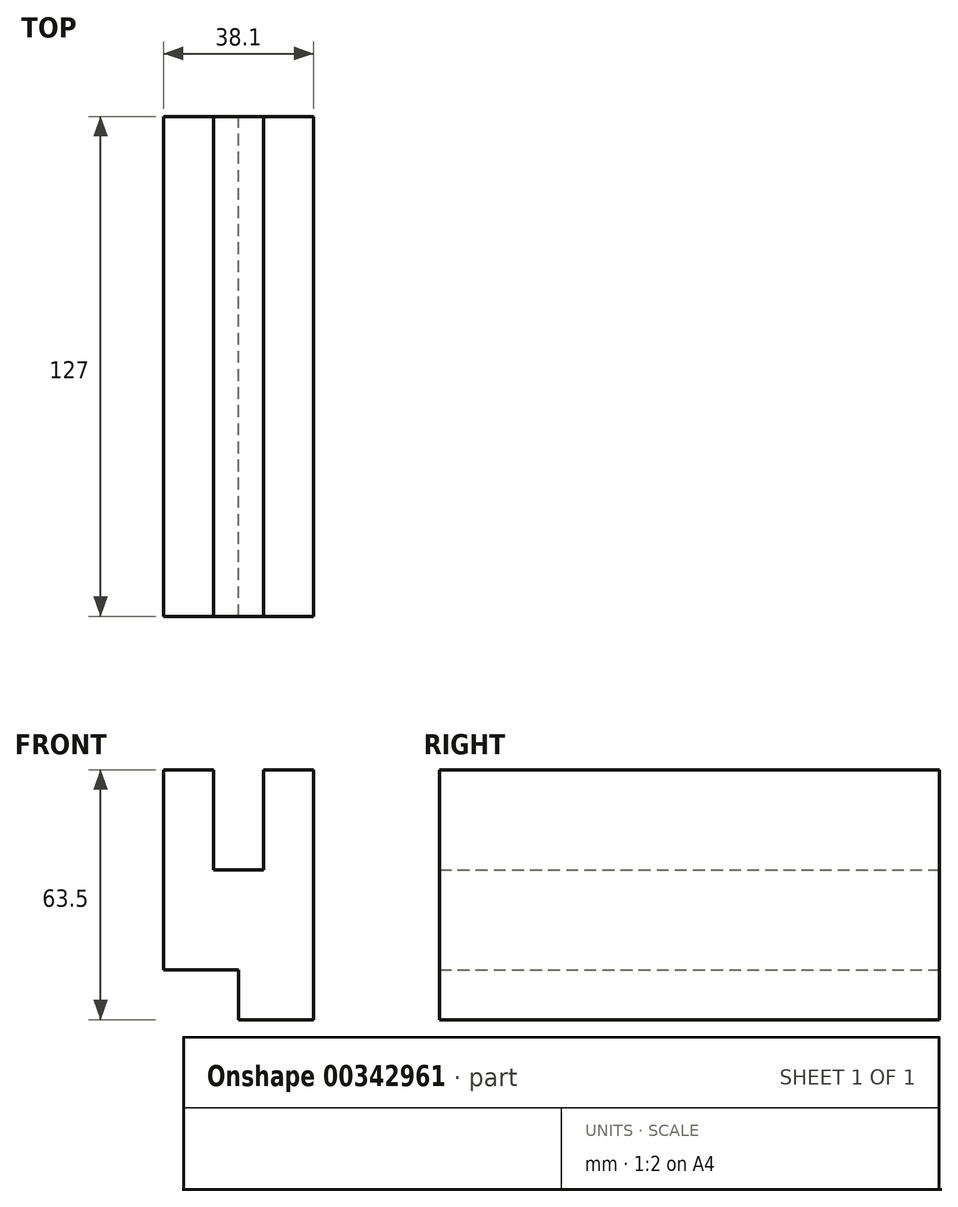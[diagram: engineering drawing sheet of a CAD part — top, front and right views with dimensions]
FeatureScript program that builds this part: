
annotation { "Feature Type Name" : "Feature", "Feature Type Description" : "" }
export const myFeature = defineFeature(function(context is Context, id is Id, definition is map)
    precondition{}
    {
        {
            var Q0;
            Q0=qCreatedBy(makeId("Front.planeOp"),FACE);
            var sketch = newSketch(context, id + "F0", { "sketchPlane" : qUnion([Q0])});
            skLineSegment(sketch, "E0", {"start": v(-56.74, -21.71) * mm, "end": v(-37.7, -21.71) * mm});
            skLineSegment(sketch, "E1", {"start": v(-37.7, -21.71) * mm, "end": v(-37.7, -34.41) * mm});
            skLineSegment(sketch, "E2", {"start": v(-37.7, -34.41) * mm, "end": v(-18.64, -34.41) * mm});
            skLineSegment(sketch, "E3", {"start": v(-18.64, -34.41) * mm, "end": v(-18.64, 29.09) * mm});
            skLineSegment(sketch, "E4", {"start": v(-18.64, 29.09) * mm, "end": v(-31.34, 29.09) * mm});
            skLineSegment(sketch, "E5", {"start": v(-31.34, 29.09) * mm, "end": v(-31.34, 3.69) * mm});
            skLineSegment(sketch, "E6", {"start": v(-31.34, 3.69) * mm, "end": v(-44.04, 3.69) * mm});
            skLineSegment(sketch, "E7", {"start": v(-44.04, 3.69) * mm, "end": v(-44.04, 29.09) * mm});
            skLineSegment(sketch, "E8", {"start": v(-44.04, 29.09) * mm, "end": v(-56.74, 29.09) * mm});
            skLineSegment(sketch, "E9", {"start": v(-56.74, 29.09) * mm, "end": v(-56.74, -21.71) * mm});
            skSolve(sketch);
        }
        {
            var Q0;
            Q0 = qSketchRegion(id + "F0", true);
            extrude(context, id + "F1", {"entities" : qUnion([Q0]), "depth" : 127 * mm});
        }
    });
